# Revit family: Monza_ Table Square  h73
name_source: partatom
category: Furniture
revit_build: Autodesk Revit 2017 (Build: 20160225_1515(x64)
units: mm (PartAtom-declared; Revit-internal decimal feet)

## family parameters
Cut with Voids When Loaded = No
Host = Face
Room Calculation Point = No
Shared = No

## types (1)
- Monza_ Table Square  h73
    Anti-slip rubber = Plank - Anti-slip rubber
    BIMobject category = Tables
    BIMobject category code = furniture-tables
    BIMobject main category = Furniture
    BIMobject main category code = furniture
    Brand url = http://www.plank.it
    Data sheet = https://www.plank.it
    Date of publishing = 1/1/2016
    Default Elevation = 1219 mm
    Description = Table system. Aluminum structure with white or black powder coating, aluminum legs with white or black powder coating or natural ash veneer surface, table top in white or black high pressure laminate (HPL). For Indoor and Outdoor use (powder-coated leg version only).
    Design country = Italy
    Edition number = 1
    IFC Classification = Furnishing Element
    Legs = Plank - 
Aluminum veneered varnished ash
    Manufacturer = Plank S.r.l.  - Ora (BZ)
    Manufacturer country = Italy
    Manufacturer name = PLANK
    Masterformat 2014 Code = 12 00 00
    Masterformat 2014 Description = Furnishings
    Material main = Aluminium
    Material secondary = Laminate
    Model = Monza_ Table Square  h73
    NBS Reference Code = 31
    NBS Reference Description = Fittings, Furnishings And Equipment (Ff&E) Products
    Nominal height = 730 mm  [stored 2.39501 ft]
    Nominal width = 0 mm  [stored 0 ft]
    OmniClass Code = 23-21 00 00
    OmniClass Description = Furnishings, Fixtures and Equipment Products
    Product Guid = 3459dbb5-5bee-4c24-b3a9-f4581a13cbf9
    Product SKU = monza_chair
    Product data url = https://bimobject.com
    Product family = Monza
    Product group = Table
    Product url = https://www.plank.it
    QR code = http://bimobject.com
    Shape = Square
    Table Top = Plank - Laminato HPL
    Technical description = https://www.plank.it
    Type = Forniture
    UNSPSC Code = 56
    URL = https://www.plank.it
    Uniclass 1.4 Code = JN
    Uniclass 1.4 Description = Furniture/Equipment
    Uniclass 2.0 Code = EE-35
    Uniclass 2.0 Description = Fittings, Furnishings And Equipment (Ff&E) And Signage Elements
    Uniclass 2015 Code = EF_40_30
    Uniclass 2015 Name = Furnishings
    Uniformat II Code = E2020
    Uniformat II Description = Movable Furnishings
    Weight Net (Kg) = 0

note: [stored X ft] marks values corroborated as IEEE doubles in the binary element streams (Revit-internal decimal feet)
